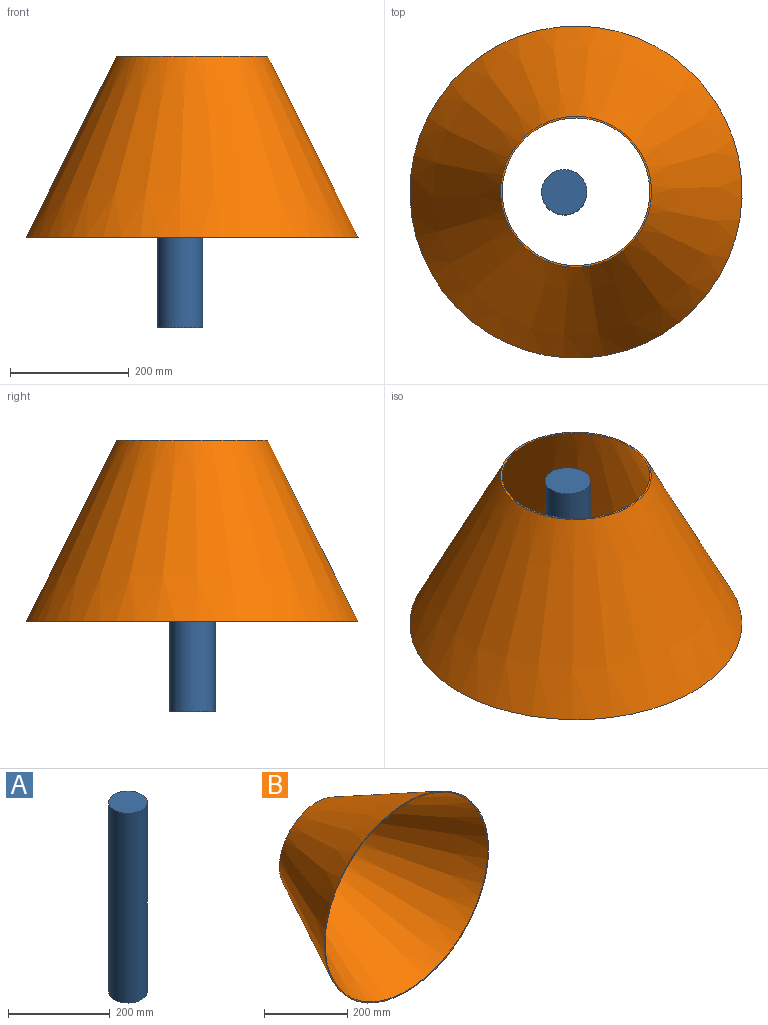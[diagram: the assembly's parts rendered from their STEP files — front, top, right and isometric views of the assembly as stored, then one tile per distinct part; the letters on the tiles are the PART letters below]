
ASSEMBLY  parts=2 mates=1
PART A: 3 faces, bbox 76.2x76.2x457.2 mm
  f0: cylinder r=38.1mm len=457.2mm, axis (0,0,-1), area 109448.8mm2, adj f1,f2
  f1: plane 76.2x76.2mm, normal (0,0,1), area 4560.4mm2, adj f0
  f2: plane 76.2x76.2mm, normal (0,0,-1), area 4560.4mm2, adj f0
PART B: 4 faces, bbox 558.8x304.8x558.8 mm
  f0: plane 558.8x558.8mm, normal (0,-1,0), area 4960mm2, adj f1,f3
  f1: cone r=127mm half-angle=26.6deg, axis (0,-1,0), area 435084.4mm2, adj f0,f2
  f2: plane 254x254mm, normal (0,1,0), area 2240.7mm2, adj f1,f3
  f3: cone r=124.73mm half-angle=26.6deg, axis (0,-1,0), area 429003.9mm2, adj f0,f2
PLACE A rot(axis=(0,0,1),43.6deg) t=(91.93,-45.93,143.45)mm
PLACE B rot(axis=(0.29,0.68,0.68),147.7deg) t=(111.78,-45.48,295.85)mm
MATE planar B.f1 <-> A.f0  axis (0,0,1) through (111.78,-45.48,600.65)mm
